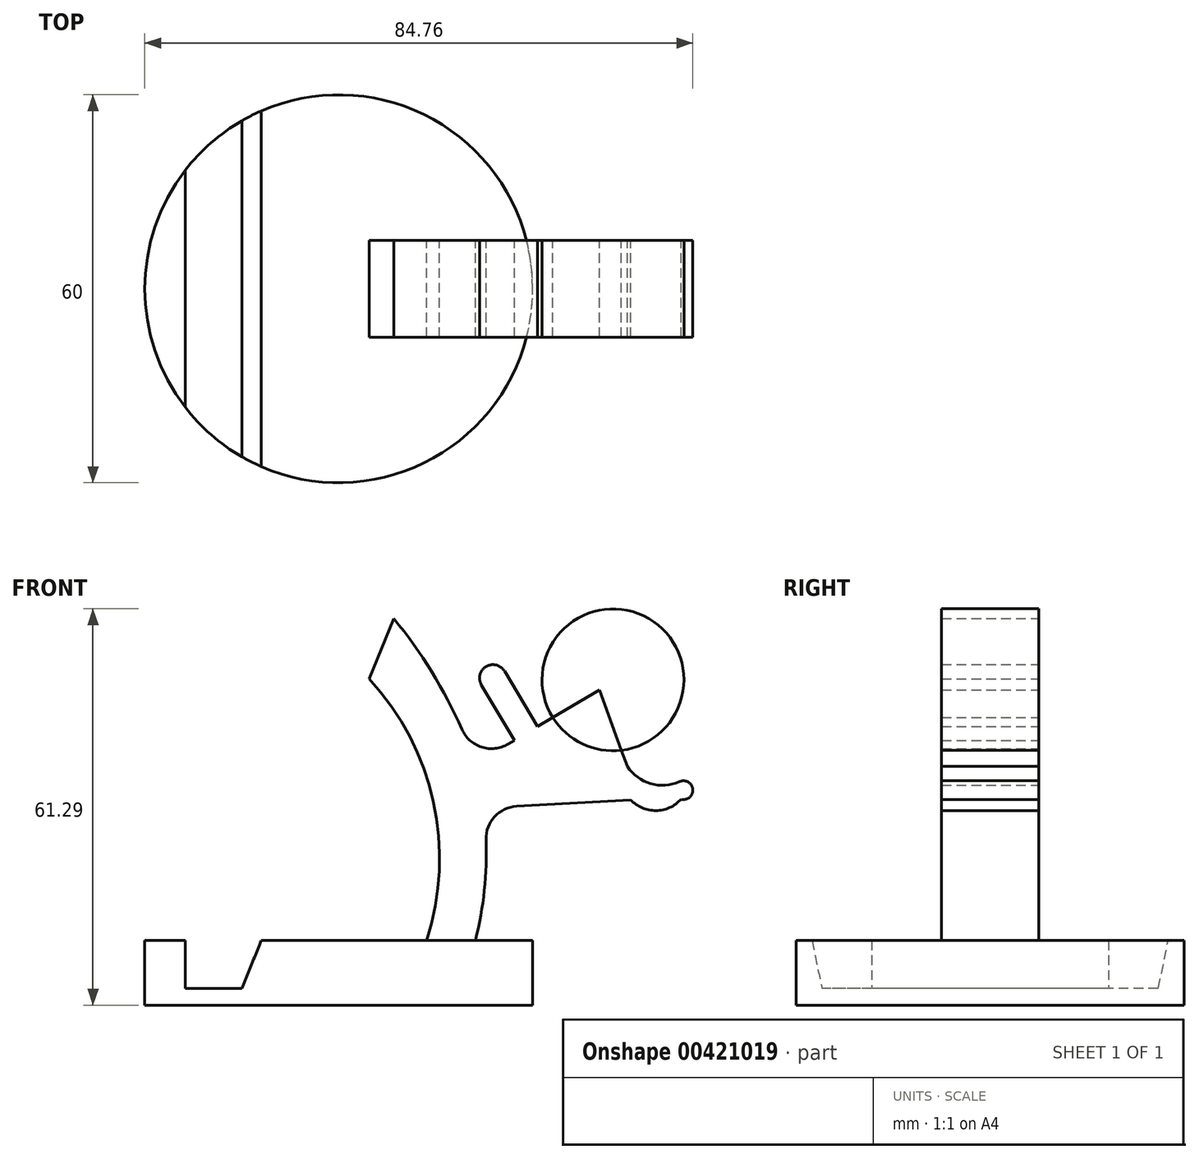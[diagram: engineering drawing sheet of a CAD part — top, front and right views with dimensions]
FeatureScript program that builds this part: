
annotation { "Feature Type Name" : "Feature", "Feature Type Description" : "" }
export const myFeature = defineFeature(function(context is Context, id is Id, definition is map)
    precondition{}
    {
        {
            var Q0;
            Q0=qCreatedBy(makeId("Top.planeOp"),FACE);
            var sketch = newSketch(context, id + "F0", { "sketchPlane" : qUnion([Q0])});
            skCircle(sketch, "E0", {"center": v(0, 0) * mm, "radius": 30 * mm});
            skSolve(sketch);
        }
        {
            var Q0;
            Q0 = qSketchRegion(id + "F0", true);
            extrude(context, id + "F1", {"entities" : qUnion([Q0]), "depth" : 10 * mm});
        }
        {
            var Q0;
            Q0=qCreatedBy(makeId("Front.planeOp"),FACE);
            var sketch = newSketch(context, id + "F2", { "sketchPlane" : qUnion([Q0])});
            skLineSegment(sketch, "E1", {"start": v(-16.07, 0) * mm, "end": v(9.79, 62.89) * mm});
            skArc(sketch, "E2", {"start": v(21.14, 10) * mm, "mid": v(22.51, 17.74) * mm, "end": v(22.8, 25.6) * mm});
            skArc(sketch, "E3", {"start": v(13.58, 10) * mm, "mid": v(14.63, 31.44) * mm, "end": v(4.69, 50.48) * mm});
            skLineSegment(sketch, "E4", {"start": v(13.58, 10) * mm, "end": v(21.14, 10) * mm});
            skLineSegment(sketch, "E5", {"start": v(27.51, 30.76) * mm, "end": v(46.48, 31.83) * mm});
            skLineSegment(sketch, "E6", {"start": v(46.48, 31.83) * mm, "end": v(40.32, 48.77) * mm});
            skLineSegment(sketch, "E7", {"start": v(40.32, 48.77) * mm, "end": v(26.18, 40.37) * mm});
            skCircle(sketch, "E8", {"center": v(42.42, 50.31) * mm, "radius": 10.97 * mm});
            skLineSegment(sketch, "E9", {"start": v(30.73, 43.07) * mm, "end": v(25.63, 51.64) * mm});
            skLineSegment(sketch, "E10", {"start": v(25.63, 51.64) * mm, "end": v(22.08, 49.53) * mm});
            skLineSegment(sketch, "E11", {"start": v(22.08, 49.53) * mm, "end": v(27.17, 40.96) * mm});
            skArc(sketch, "E12", {"start": v(44.62, 36.94) * mm, "mid": v(48.23, 34.26) * mm, "end": v(52.71, 34.57) * mm});
            skArc(sketch, "E13", {"start": v(45.16, 31.76) * mm, "mid": v(49.07, 30.09) * mm, "end": v(52.95, 31.83) * mm});
            skLineSegment(sketch, "E14", {"start": v(52.71, 34.57) * mm, "end": v(52.95, 31.83) * mm});
            skArc(sketch, "E15", {"start": v(52.95, 31.83) * mm, "mid": v(54.75, 33.37) * mm, "end": v(52.71, 34.57) * mm});
            skArc(sketch, "E16", {"start": v(25.63, 51.64) * mm, "mid": v(22.8, 52.36) * mm, "end": v(22.08, 49.53) * mm});
            skArc(sketch, "E17.filletArc", {"start": v(27.51, 30.76) * mm, "mid": v(24.1, 29.14) * mm, "end": v(22.8, 25.6) * mm});
            skArc(sketch, "E18", {"start": v(19.05, 42.65) * mm, "mid": v(14.37, 51.58) * mm, "end": v(8.5, 59.78) * mm});
            skPoint(sketch, "E19.visualSharp", {"position": v(21.14, 37.37) * mm});
            skArc(sketch, "E19.filletArc", {"start": v(19.05, 42.65) * mm, "mid": v(22.1, 39.9) * mm, "end": v(26.18, 40.37) * mm});
            skLineSegment(sketch, "E20", {"start": v(-15, 2.6) * mm, "end": v(-23.75, 2.6) * mm});
            skLineSegment(sketch, "E21", {"start": v(-23.75, 2.6) * mm, "end": v(-23.75, 10.61) * mm});
            skLineSegment(sketch, "E22", {"start": v(-23.75, 10.61) * mm, "end": v(-11.7, 10.61) * mm});
            skSolve(sketch);
        }
        {
            var Q0;
            {var subQ0=sQuery(id+"F2.wireOp",EDGE,"E20");Q0=makeQuery(id+"F2.imprint","IMPRINT",FACE,{"disambiguationData":[TD([[makeQuery(id+"F2.imprint","IMPRINT",EDGE,{"derivedFrom":subQ0}),-1.0]])]});}
            extrude(context, id + "F3", {"entities" : qUnion([Q0]), "operationType" : NewBodyOperationType.REMOVE, "endBound" : BoundingType.SYMMETRIC, "oppositeDirection" : true, "depth" : 73.2 * mm});
        }
        {
            var Q0;
            Q0=makeQuery(id+"F2.imprint","IMPRINT",FACE,{"disambiguationData":[TD([[makeQuery(id+"F2.imprint","IMPRINT",EDGE,{"derivedFrom":sQuery(id+"F2.wireOp",EDGE,"E2")}),1.0]])]});
            extrude(context, id + "F4", {"entities" : qUnion([Q0]), "operationType" : NewBodyOperationType.ADD, "endBound" : BoundingType.SYMMETRIC, "depth" : 15 * mm});
        }
        {
            var Q0;
            {var subQ0=sQuery(id+"F2.wireOp",EDGE,"E7");var subQ1=sQuery(id+"F2.wireOp",EDGE,"E6");var subQ2=makeQuery(id+"F2.imprint","INTERSECT",VERTEX,{"derivedFrom":[subQ1,subQ0]});Q0=makeQuery(id+"F2.imprint","IMPRINT",FACE,{"disambiguationData":[TD([[makeQuery(id+"F2.imprint","IMPRINT",EDGE,{"disambiguationData":[TD([[subQ2,1.0]])],"derivedFrom":subQ1}),-1.0]])]});}
            extrude(context, id + "F5", {"entities" : qUnion([Q0]), "endBound" : BoundingType.SYMMETRIC, "depth" : 15 * mm});
        }
        {
            var Q0;
            {var subQ0=sQuery(id+"F2.wireOp",EDGE,"E7");var subQ1=sQuery(id+"F2.wireOp",EDGE,"E6");var subQ2=makeQuery(id+"F2.imprint","INTERSECT",VERTEX,{"derivedFrom":[subQ1,subQ0]});Q0=makeQuery(id+"F2.imprint","IMPRINT",FACE,{"disambiguationData":[TD([[makeQuery(id+"F2.imprint","IMPRINT",EDGE,{"disambiguationData":[TD([[subQ2,1.0]])],"derivedFrom":subQ1}),1.0]])]});}
            extrude(context, id + "F6", {"entities" : qUnion([Q0]), "endBound" : BoundingType.SYMMETRIC, "depth" : 15 * mm});
        }
        {
            var Q0;
            {var subQ0=sQuery(id+"F2.wireOp",EDGE,"E9");Q0=makeQuery(id+"F2.imprint","IMPRINT",FACE,{"disambiguationData":[TD([[makeQuery(id+"F2.imprint","IMPRINT",EDGE,{"derivedFrom":subQ0}),1.0]])]});}
            extrude(context, id + "F7", {"entities" : qUnion([Q0]), "operationType" : NewBodyOperationType.ADD, "endBound" : BoundingType.SYMMETRIC, "depth" : 15 * mm});
        }
        {
            var Q0;
            Q0=makeQuery(id+"F2.imprint","IMPRINT",FACE,{"disambiguationData":[TD([[makeQuery(id+"F2.imprint","IMPRINT",EDGE,{"derivedFrom":sQuery(id+"F2.wireOp",EDGE,"E10")}),-1.0]])]});
            extrude(context, id + "F8", {"entities" : qUnion([Q0]), "operationType" : NewBodyOperationType.ADD, "endBound" : BoundingType.SYMMETRIC, "depth" : 15 * mm});
        }
        {
            var Q0;
            {var subQ1=sQuery(id+"F2.wireOp",EDGE,"E12");Q0=makeQuery(id+"F2.imprint","IMPRINT",FACE,{"disambiguationData":[TD([[makeQuery(id+"F2.imprint","IMPRINT",EDGE,{"derivedFrom":subQ1}),-1.0]])]});}
            extrude(context, id + "F9", {"entities" : qUnion([Q0]), "operationType" : NewBodyOperationType.ADD, "endBound" : BoundingType.SYMMETRIC, "depth" : 15 * mm});
        }
        {
            var Q0;
            Q0=makeQuery(id+"F2.imprint","IMPRINT",FACE,{"disambiguationData":[TD([[makeQuery(id+"F2.imprint","IMPRINT",EDGE,{"derivedFrom":sQuery(id+"F2.wireOp",EDGE,"E14")}),1.0]])]});
            extrude(context, id + "F10", {"entities" : qUnion([Q0]), "operationType" : NewBodyOperationType.ADD, "endBound" : BoundingType.SYMMETRIC, "depth" : 15 * mm});
        }
    });
